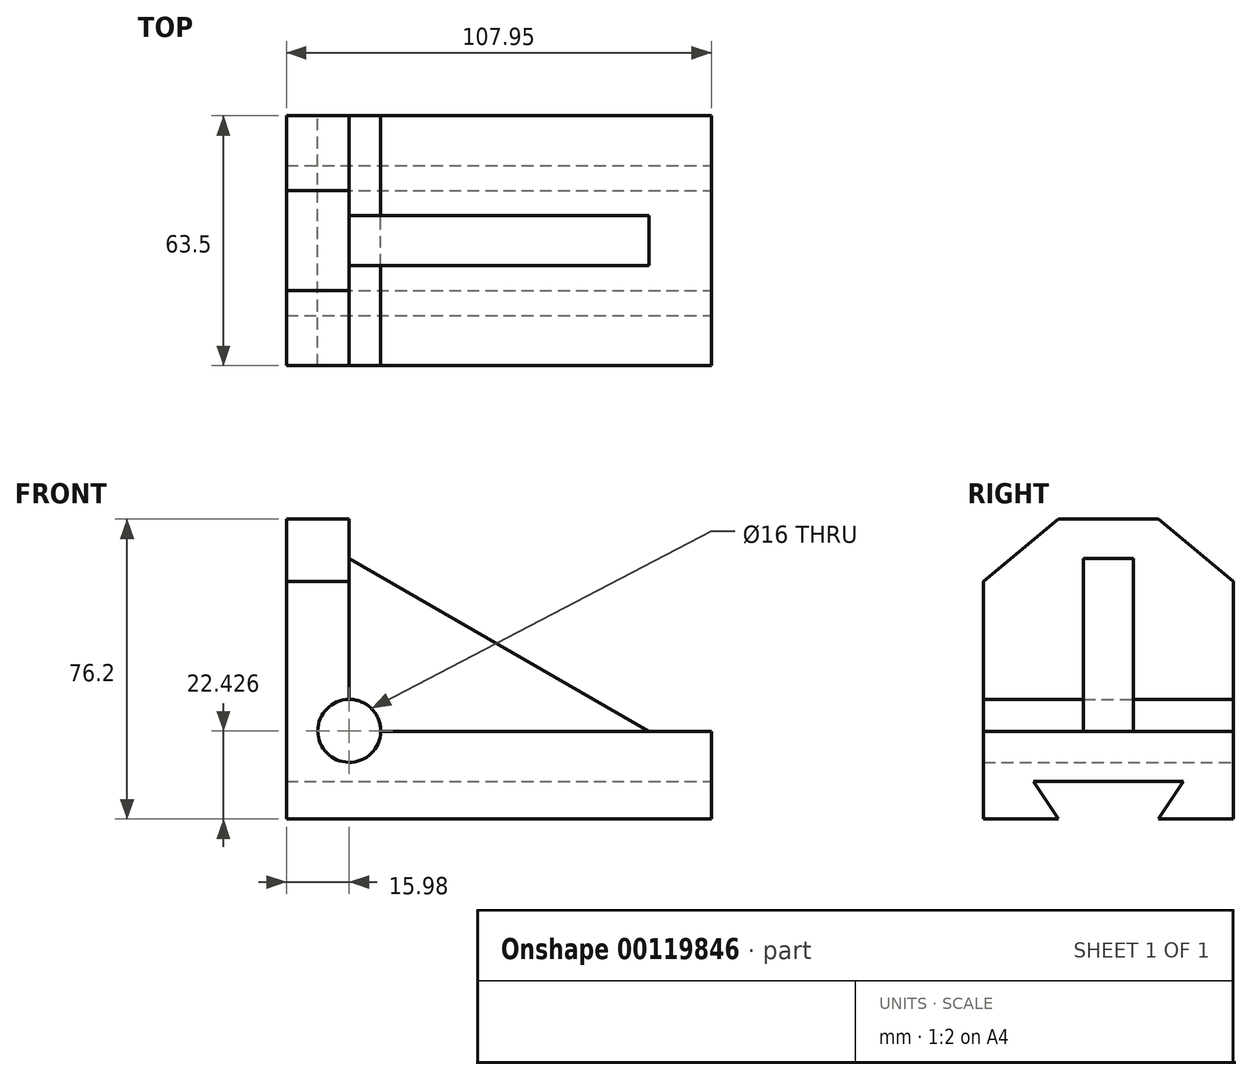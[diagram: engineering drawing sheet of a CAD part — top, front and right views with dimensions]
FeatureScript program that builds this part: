
annotation { "Feature Type Name" : "Feature", "Feature Type Description" : "" }
export const myFeature = defineFeature(function(context is Context, id is Id, definition is map)
    precondition{}
    {
        {
            var Q0;
            Q0=qCreatedBy(makeId("Front.planeOp"),FACE);
            var sketch = newSketch(context, id + "F0", { "sketchPlane" : qUnion([Q0])});
            skLineSegment(sketch, "E0", {"start": v(0, 0) * mm, "end": v(107.95, 0) * mm});
            skLineSegment(sketch, "E1", {"start": v(107.95, 0) * mm, "end": v(107.95, 22.23) * mm});
            skLineSegment(sketch, "E2", {"start": v(107.95, 22.23) * mm, "end": v(15.88, 22.23) * mm});
            skLineSegment(sketch, "E3", {"start": v(15.88, 22.22) * mm, "end": v(15.88, 76.2) * mm});
            skLineSegment(sketch, "E4", {"start": v(15.88, 76.2) * mm, "end": v(0, 76.2) * mm});
            skLineSegment(sketch, "E5", {"start": v(0, 76.2) * mm, "end": v(0, 0) * mm});
            skSolve(sketch);
        }
        {
            var Q0;
            Q0=makeQuery(id+"F0.imprint","IMPRINT",FACE,{"disambiguationData":[TD([[makeQuery(id+"F0.imprint","IMPRINT",EDGE,{"derivedFrom":sQuery(id+"F0.wireOp",EDGE,"E0")}),1.0]])]});
            extrude(context, id + "F1", {"entities" : qUnion([Q0]), "endBound" : BoundingType.SYMMETRIC, "depth" : 63.5 * mm});
        }
        {
            var Q0;
            Q0=makeQuery(id+"F1.opExtrude","SWEPT_FACE",FACE,{"disambiguationData":[OSD([sQuery(id+"F0.wireOp",EDGE,"E1")])]});
            var sketch = newSketch(context, id + "F2", { "sketchPlane" : qUnion([Q0])});
            skLineSegment(sketch, "E6", {"start": v(12.7, 0) * mm, "end": v(19.05, 9.52) * mm});
            skLineSegment(sketch, "E7", {"start": v(19.05, 9.52) * mm, "end": v(-19.05, 9.52) * mm});
            skLineSegment(sketch, "E8", {"start": v(-19.05, 9.52) * mm, "end": v(-12.7, 0) * mm});
            skLineSegment(sketch, "E9", {"start": v(-12.7, 0) * mm, "end": v(12.7, 0) * mm});
            skSolve(sketch);
        }
        {
            var Q0;
            Q0=makeQuery(id+"F2.imprint","IMPRINT",FACE,{"disambiguationData":[TD([[makeQuery(id+"F2.imprint","IMPRINT",EDGE,{"derivedFrom":sQuery(id+"F2.wireOp",EDGE,"E6")}),1.0]])]});
            extrude(context, id + "F3", {"entities" : qUnion([Q0]), "operationType" : NewBodyOperationType.REMOVE, "endBound" : BoundingType.THROUGH_ALL, "oppositeDirection" : true, "depth" : 25.4 * mm});
        }
        {
            var Q0;
            Q0=qCreatedBy(makeId("Front.planeOp"),FACE);
            var sketch = newSketch(context, id + "F4", { "sketchPlane" : qUnion([Q0])});
            skLineSegment(sketch, "E10", {"start": v(15.87, 66.22) * mm, "end": v(15.88, 22.22) * mm});
            skLineSegment(sketch, "E11", {"start": v(15.88, 22.22) * mm, "end": v(92.08, 22.23) * mm});
            skLineSegment(sketch, "E12", {"start": v(92.08, 22.23) * mm, "end": v(15.88, 66.22) * mm});
            skSolve(sketch);
        }
        {
            var Q0;
            Q0=makeQuery(id+"F4.imprint","IMPRINT",FACE,{"disambiguationData":[TD([[makeQuery(id+"F4.imprint","IMPRINT",EDGE,{"derivedFrom":sQuery(id+"F4.wireOp",EDGE,"E10")}),1.0]])]});
            extrude(context, id + "F5", {"entities" : qUnion([Q0]), "operationType" : NewBodyOperationType.ADD, "endBound" : BoundingType.SYMMETRIC, "depth" : 12.7 * mm});
        }
        {
            var Q0;
            Q0=makeQuery(id+"F1.opExtrude","SWEPT_FACE",FACE,{"disambiguationData":[OSD([sQuery(id+"F0.wireOp",EDGE,"E5")])]});
            var sketch = newSketch(context, id + "F6", { "sketchPlane" : qUnion([Q0])});
            skLineSegment(sketch, "E13", {"start": v(-12.7, 76.2) * mm, "end": v(-31.75, 76.2) * mm});
            skLineSegment(sketch, "E14", {"start": v(-31.75, 76.2) * mm, "end": v(-31.75, 60.33) * mm});
            skLineSegment(sketch, "E15", {"start": v(-31.75, 60.33) * mm, "end": v(-12.7, 76.2) * mm});
            skLineSegment(sketch, "E16.MirrorCS", {"start": v(12.7, 76.2) * mm, "end": v(31.75, 76.2) * mm});
            skLineSegment(sketch, "E17.MirrorCS", {"start": v(31.75, 76.2) * mm, "end": v(31.75, 60.33) * mm});
            skLineSegment(sketch, "E18.MirrorCS", {"start": v(31.75, 60.33) * mm, "end": v(12.7, 76.2) * mm});
            skSolve(sketch);
        }
        {
            var Q0;
            Q0 = qSketchRegion(id + "F6", true);
            extrude(context, id + "F7", {"entities" : qUnion([Q0]), "operationType" : NewBodyOperationType.REMOVE, "endBound" : BoundingType.SYMMETRIC, "oppositeDirection" : true, "depth" : 76.2 * mm});
        }
        {
            var Q0;
            Q0 = qSketchRegion(id + "F6", true);
            extrude(context, id + "F8", {"entities" : qUnion([Q0]), "operationType" : NewBodyOperationType.REMOVE, "oppositeDirection" : true, "depth" : 25.4 * mm});
        }
        {
            var Q0;
            Q0=qCreatedBy(makeId("Front.planeOp"),FACE);
            var sketch = newSketch(context, id + "F9", { "sketchPlane" : qUnion([Q0])});
            skCircle(sketch, "E19", {"center": v(15.98, 22.43) * mm, "radius": 8 * mm});
            skSolve(sketch);
        }
        {
            var Q0;
            Q0 = qSketchRegion(id + "F9", true);
            extrude(context, id + "F10", {"entities" : qUnion([Q0]), "operationType" : NewBodyOperationType.REMOVE, "endBound" : BoundingType.SYMMETRIC, "depth" : 254 * mm});
        }
    });
